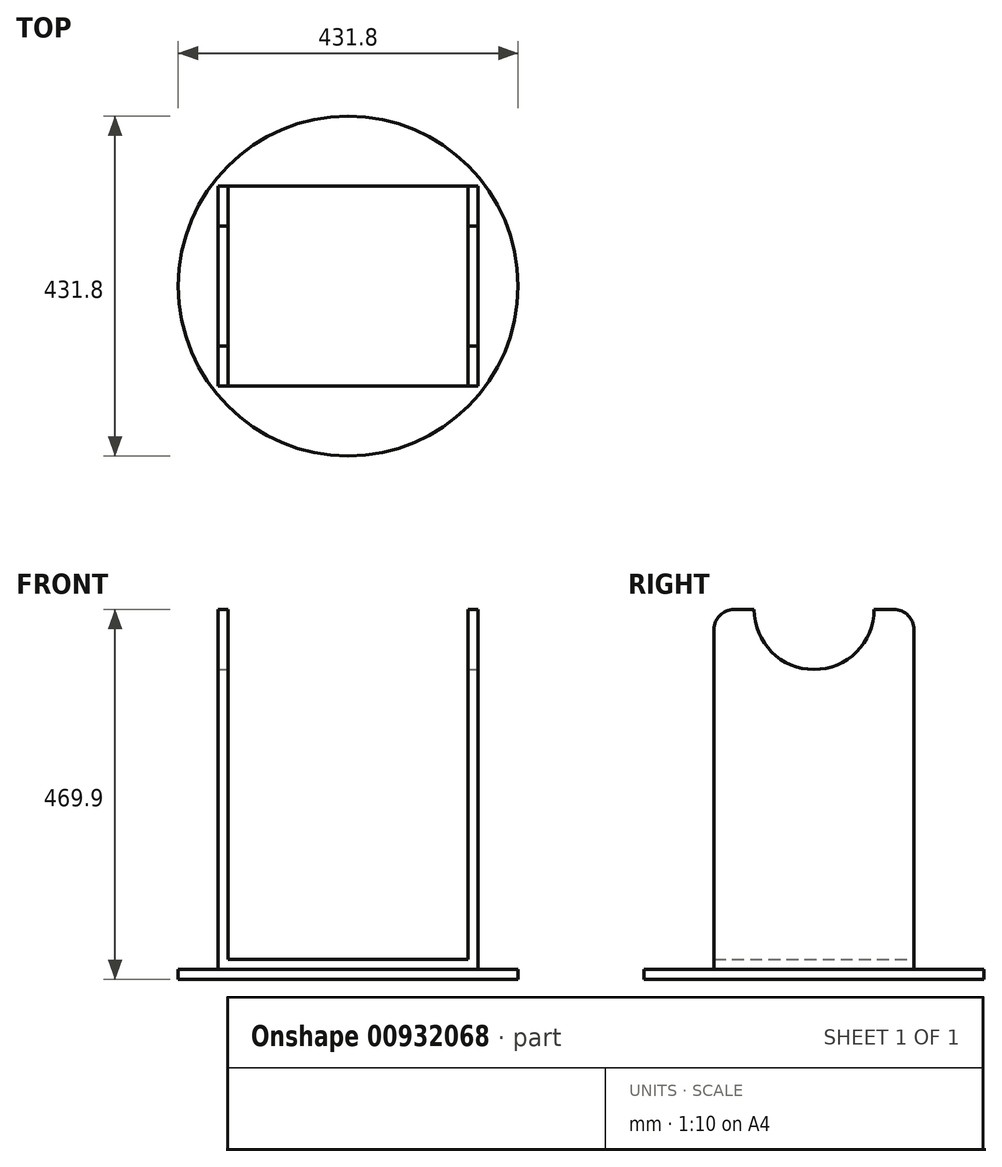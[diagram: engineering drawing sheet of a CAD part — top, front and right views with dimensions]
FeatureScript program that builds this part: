
annotation { "Feature Type Name" : "Feature", "Feature Type Description" : "" }
export const myFeature = defineFeature(function(context is Context, id is Id, definition is map)
    precondition{}
    {
        {
            var Q0;
            Q0=qCreatedBy(makeId("Front.planeOp"),FACE);
            var sketch = newSketch(context, id + "F0", { "sketchPlane" : qUnion([Q0])});
            skLineSegment(sketch, "E0", {"start": v(-152.4, 457.2) * mm, "end": v(-152.4, 12.7) * mm});
            skLineSegment(sketch, "E1", {"start": v(-152.4, 12.7) * mm, "end": v(152.4, 12.7) * mm});
            skLineSegment(sketch, "E2", {"start": v(152.4, 12.7) * mm, "end": v(152.4, 457.2) * mm});
            skLineSegment(sketch, "E3", {"start": v(152.4, 457.2) * mm, "end": v(165.1, 457.2) * mm});
            skLineSegment(sketch, "E4", {"start": v(165.1, 457.2) * mm, "end": v(165.1, 0) * mm});
            skLineSegment(sketch, "E5", {"start": v(165.1, 0) * mm, "end": v(-165.1, 0) * mm});
            skLineSegment(sketch, "E6", {"start": v(-165.1, 0) * mm, "end": v(-165.1, 457.2) * mm});
            skLineSegment(sketch, "E7", {"start": v(-165.1, 457.2) * mm, "end": v(-152.4, 457.2) * mm});
            skSolve(sketch);
        }
        {
            var Q0;
            Q0 = qSketchRegion(id + "F0", true);
            extrude(context, id + "F1", {"entities" : qUnion([Q0]), "depth" : 254 * mm, "offsetDistance" : 25.4 * mm});
        }
        {
            var Q0;
            Q0=makeQuery(id+"F1.opExtrude","SWEPT_FACE",FACE,{"disambiguationData":[OSD([sQuery(id+"F0.wireOp",EDGE,"E5")])]});
            var sketch = newSketch(context, id + "F2", { "sketchPlane" : qUnion([Q0])});
            skCircle(sketch, "E8", {"center": v(0, 127) * mm, "radius": 215.9 * mm});
            skPoint(sketch, "E8.centerSnap0", {"position": v(-165.1, 127) * mm});
            skSolve(sketch);
        }
        {
            var Q0;
            Q0 = qSketchRegion(id + "F2", true);
            extrude(context, id + "F3", {"entities" : qUnion([Q0]), "operationType" : NewBodyOperationType.ADD, "depth" : 12.7 * mm, "offsetDistance" : 25.4 * mm});
        }
        {
            var Q0;
            Q0=makeQuery(id+"F1.opExtrude","SWEPT_FACE",FACE,{"disambiguationData":[OSD([sQuery(id+"F0.wireOp",EDGE,"E4")])]});
            var sketch = newSketch(context, id + "F4", { "sketchPlane" : qUnion([Q0])});
            skArc(sketch, "E9", {"start": v(-203.2, 457.2) * mm, "mid": v(-127, 381) * mm, "end": v(-50.8, 457.2) * mm});
            skLineSegment(sketch, "E10", {"start": v(-203.2, 457.2) * mm, "end": v(-50.8, 457.2) * mm});
            skSolve(sketch);
        }
        {
            var Q0;
            Q0 = qSketchRegion(id + "F4", true);
            extrude(context, id + "F5", {"entities" : qUnion([Q0]), "operationType" : NewBodyOperationType.REMOVE, "endBound" : BoundingType.THROUGH_ALL, "oppositeDirection" : true, "depth" : 25.4 * mm, "offsetDistance" : 25.4 * mm});
        }
        {
            var Q0;
            Q0=makeQuery(id+"F1.opExtrude","CAP_EDGE",EDGE,{"disambiguationData":[OSD([sQuery(id+"F0.wireOp",EDGE,"E3")])],"isStart":false});
            var Q1;
            Q1=makeQuery(id+"F1.opExtrude","CAP_EDGE",EDGE,{"disambiguationData":[OSD([sQuery(id+"F0.wireOp",EDGE,"E3")])],"isStart":true});
            var Q2;
            Q2=makeQuery(id+"F1.opExtrude","CAP_EDGE",EDGE,{"disambiguationData":[OSD([sQuery(id+"F0.wireOp",EDGE,"E7")])],"isStart":true});
            var Q3;
            Q3=makeQuery(id+"F1.opExtrude","CAP_EDGE",EDGE,{"disambiguationData":[OSD([sQuery(id+"F0.wireOp",EDGE,"E7")])],"isStart":false});
            fillet(context, id + "F6", {"entities" : qUnion([Q0, Q1, Q2, Q3]), "radius" : 25.4 * mm, "tangentPropagation" : true, "allowEdgeOverflow" : false});
        }
    });
